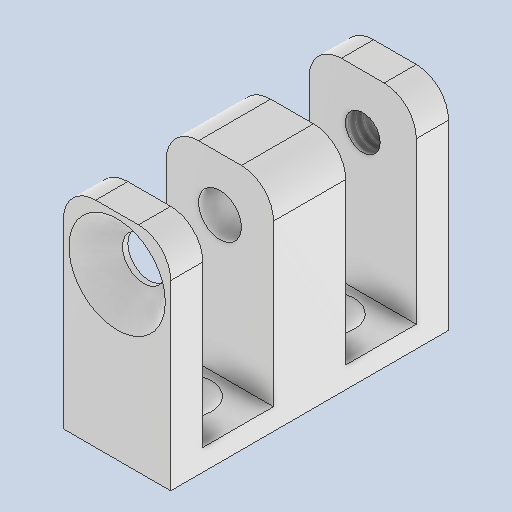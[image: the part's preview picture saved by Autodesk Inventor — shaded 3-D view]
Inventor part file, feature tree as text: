
AUTODESK INVENTOR PART (.ipt)
format: ipt  version: 2025 (Build 290162010, 162A)  size: 216,064 bytes
history: native  units: mm
features: sketch x5, hole x3, extrude x2, fillet x1
ambient origin geometry x8: Origin, YZ Plane, XZ Plane, XY Plane, X Axis, Y Axis, Z Axis, Center Point
bodies: Volumenkörper1 (feature_tree)
feature tree (11):
  extrude  "Extrusion1"  Depth=3.0mm
  fillet  "Rundung1"  Radius=3.0mm
  hole  "Bohrung1"  [1 undecoded]
  extrude  "Extrusion2"  Depth=2.0mm
  hole  "Bohrung2"  [1 undecoded]
  hole  "Bohrung3"  [1 undecoded]
  sketch  "Skizze1"  dims[d0=10.0mm d1=3.0mm d2=3.0mm]
  sketch  "Skizze2"  dims[d5=20.0mm d6=0.0mm d7=3.0mm]
  sketch  "Skizze3"  dims[d8=3.242mm d9=8.0mm d10=9.0mm d11=14.0mm d12=90.0deg d13=11.8mm d14=20.594885mm d15=2.0mm]
  sketch  "Skizze4"  dims[d16=20.0mm d17=0.0mm]
  sketch  "Skizze5"  dims[d19=2.0mm d20=8.0mm d21=5.0mm d22=2.0mm d23=90.0deg d24=8.0mm d25=20.594885mm d26=4.0mm d27=8.0mm d28=4.0mm d29=2.0mm d30=90.0deg d31=5.0mm d32=0.0mm d34=13.333333mm d35=25.933333mm d38=6.6mm d39=6.733333mm]
note: 3 required parameter values undecoded (feature->parameter linkage not recoverable at this tier; creation-order binding heuristic only, values carry confidence <= 0.55)
